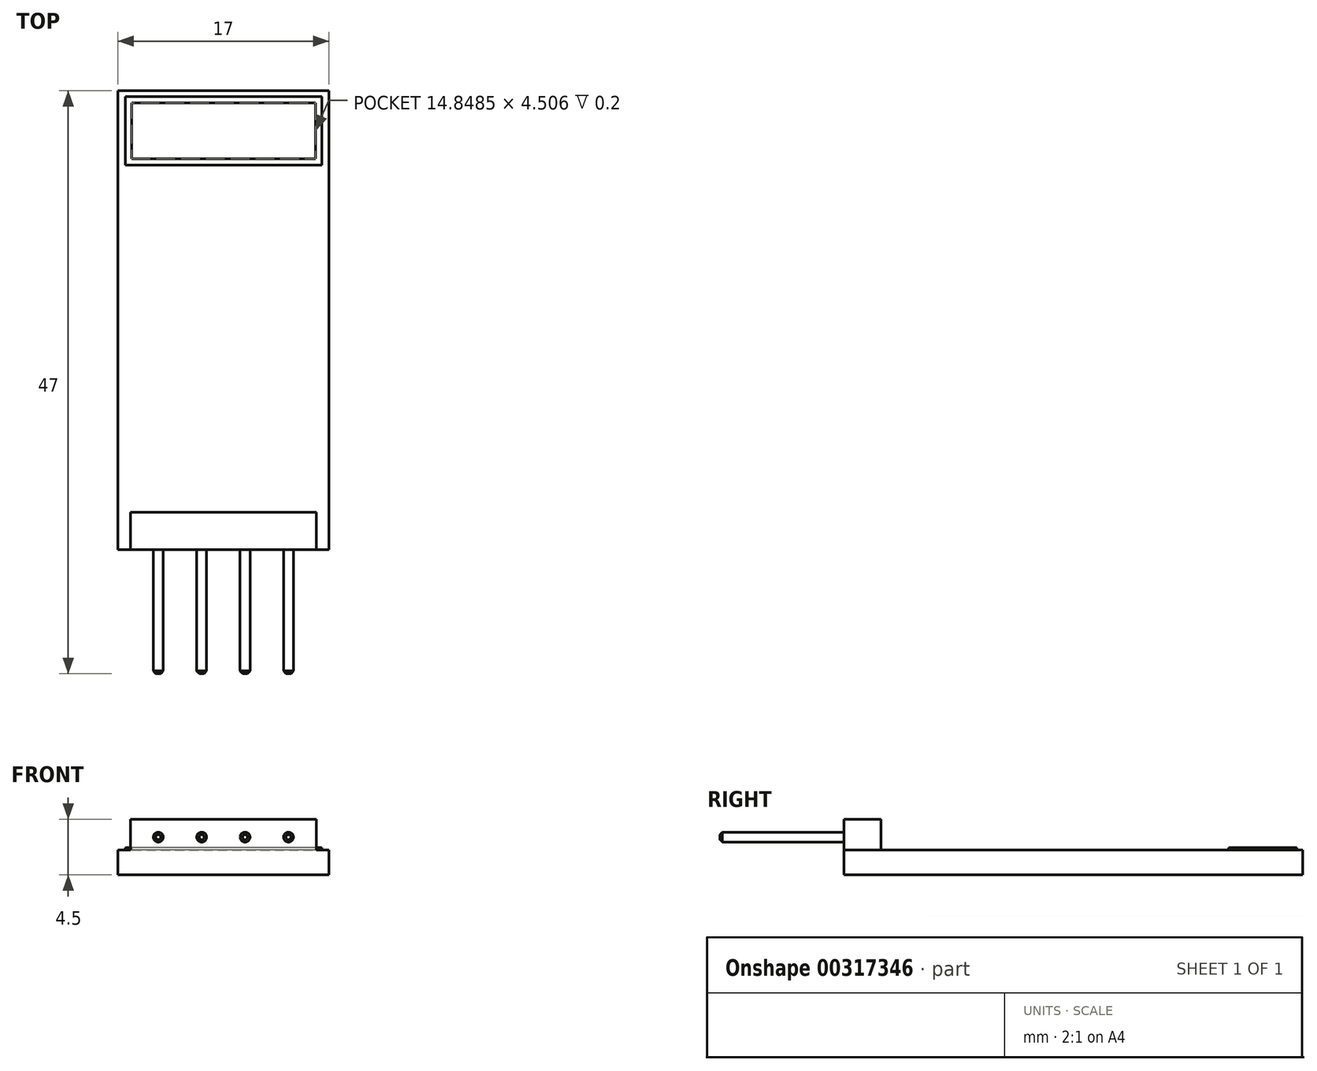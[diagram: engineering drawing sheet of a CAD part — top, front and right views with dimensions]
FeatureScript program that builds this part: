
annotation { "Feature Type Name" : "Feature", "Feature Type Description" : "" }
export const myFeature = defineFeature(function(context is Context, id is Id, definition is map)
    precondition{}
    {
        {
            var Q0;
            Q0=qCreatedBy(makeId("Top.planeOp"),FACE);
            var sketch = newSketch(context, id + "F0", { "sketchPlane" : qUnion([Q0])});
            skLineSegment(sketch, "E0.bottom", {"start": v(-8.5, 18.5) * mm, "end": v(8.5, 18.5) * mm});
            skLineSegment(sketch, "E0.top", {"start": v(-8.5, -18.5) * mm, "end": v(8.5, -18.5) * mm});
            skLineSegment(sketch, "E0.left", {"start": v(-8.5, 18.5) * mm, "end": v(-8.5, -18.5) * mm});
            skLineSegment(sketch, "E0.right", {"start": v(8.5, 18.5) * mm, "end": v(8.5, -18.5) * mm});
            skSolve(sketch);
        }
        {
            var Q0;
            Q0=makeQuery(id+"F0.imprint","IMPRINT",FACE,{"disambiguationData":[TD([[makeQuery(id+"F0.imprint","IMPRINT",EDGE,{"derivedFrom":sQuery(id+"F0.wireOp",EDGE,"E0.bottom")}),-1.0]])]});
            extrude(context, id + "F1", {"entities" : qUnion([Q0]), "endBound" : BoundingType.SYMMETRIC, "depth" : 2 * mm});
        }
        {
            var Q0;
            Q0=makeQuery(id+"F1.opExtrude","CAP_FACE",FACE,{"disambiguationData":[OSD([sQuery(id+"F0.wireOp",EDGE,"E0.bottom"),sQuery(id+"F0.wireOp",EDGE,"E0.top"),sQuery(id+"F0.wireOp",EDGE,"E0.left"),sQuery(id+"F0.wireOp",EDGE,"E0.right")])],"isStart":false});
            var sketch = newSketch(context, id + "F2", { "sketchPlane" : qUnion([Q0])});
            skLineSegment(sketch, "E1.bottom", {"start": v(-7.5, -18.5) * mm, "end": v(7.5, -18.5) * mm});
            skLineSegment(sketch, "E1.top", {"start": v(-7.5, -15.5) * mm, "end": v(7.5, -15.5) * mm});
            skLineSegment(sketch, "E1.left", {"start": v(-7.5, -18.5) * mm, "end": v(-7.5, -15.5) * mm});
            skLineSegment(sketch, "E1.right", {"start": v(7.5, -18.5) * mm, "end": v(7.5, -15.5) * mm});
            skSolve(sketch);
        }
        {
            var Q0;
            Q0=makeQuery(id+"F2.imprint","IMPRINT",FACE,{"disambiguationData":[TD([[makeQuery(id+"F2.imprint","IMPRINT",EDGE,{"derivedFrom":sQuery(id+"F2.wireOp",EDGE,"E1.bottom")}),1.0]])]});
            extrude(context, id + "F3", {"entities" : qUnion([Q0]), "operationType" : NewBodyOperationType.ADD, "depth" : 2.5 * mm});
        }
        {
            var Q0;
            Q0=makeQuery(id+"F3.boolean.opBoolean","MERGE",FACE,{"derivedFrom":[makeQuery(id+"F1.opExtrude","SWEPT_FACE",FACE,{"disambiguationData":[OSD([sQuery(id+"F0.wireOp",EDGE,"E0.top")])]}),makeQuery(id+"F3.opExtrude","SWEPT_FACE",FACE,{"disambiguationData":[OSD([sQuery(id+"F2.wireOp",EDGE,"E1.bottom")])]})]});
            var sketch = newSketch(context, id + "F4", { "sketchPlane" : qUnion([Q0])});
            skCircle(sketch, "E2", {"center": v(-5.25, 2.05) * mm, "radius": 0.4 * mm});
            skCircle(sketch, "E3.1.0.0", {"center": v(-1.75, 2.05) * mm, "radius": 0.4 * mm});
            skCircle(sketch, "E3.2.0.0", {"center": v(1.75, 2.05) * mm, "radius": 0.4 * mm});
            skCircle(sketch, "E3.3.0.0", {"center": v(5.25, 2.05) * mm, "radius": 0.4 * mm});
            skLineSegment(sketch, "E3.direction1", {"start": v(-5.25, 2.05) * mm, "end": v(-1.75, 2.05) * mm, "construction": true});
            skLineSegment(sketch, "E4", {"start": v(-5.25, 2.05) * mm, "end": v(-7.5, 2.05) * mm, "construction": true});
            skLineSegment(sketch, "E5", {"start": v(5.25, 2.05) * mm, "end": v(7.5, 2.05) * mm, "construction": true});
            skSolve(sketch);
        }
        {
            var Q0;
            Q0=makeQuery(id+"F4.imprint","IMPRINT",FACE,{"disambiguationData":[TD([[makeQuery(id+"F4.imprint","IMPRINT",EDGE,{"derivedFrom":sQuery(id+"F4.wireOp",EDGE,"E2")}),1.0]])]});
            var Q1;
            Q1=makeQuery(id+"F4.imprint","IMPRINT",FACE,{"disambiguationData":[TD([[makeQuery(id+"F4.imprint","IMPRINT",EDGE,{"derivedFrom":sQuery(id+"F4.wireOp",EDGE,"E3.1.0.0")}),1.0]])]});
            var Q2;
            Q2=makeQuery(id+"F4.imprint","IMPRINT",FACE,{"disambiguationData":[TD([[makeQuery(id+"F4.imprint","IMPRINT",EDGE,{"derivedFrom":sQuery(id+"F4.wireOp",EDGE,"E3.2.0.0")}),1.0]])]});
            var Q3;
            Q3=makeQuery(id+"F4.imprint","IMPRINT",FACE,{"disambiguationData":[TD([[makeQuery(id+"F4.imprint","IMPRINT",EDGE,{"derivedFrom":sQuery(id+"F4.wireOp",EDGE,"E3.3.0.0")}),1.0]])]});
            extrude(context, id + "F5", {"entities" : qUnion([Q0, Q1, Q2, Q3]), "operationType" : NewBodyOperationType.ADD, "depth" : 10 * mm});
        }
        {
            var Q0;
            Q0=makeQuery(id+"F5.opExtrude","CAP_EDGE",EDGE,{"disambiguationData":[OSD([sQuery(id+"F4.wireOp",EDGE,"E2")])],"isStart":false});
            var Q1;
            Q1=makeQuery(id+"F5.opExtrude","CAP_EDGE",EDGE,{"disambiguationData":[OSD([sQuery(id+"F4.wireOp",EDGE,"E3.1.0.0")])],"isStart":false});
            var Q2;
            Q2=makeQuery(id+"F5.opExtrude","CAP_EDGE",EDGE,{"disambiguationData":[OSD([sQuery(id+"F4.wireOp",EDGE,"E3.2.0.0")])],"isStart":false});
            var Q3;
            Q3=makeQuery(id+"F5.opExtrude","CAP_EDGE",EDGE,{"disambiguationData":[OSD([sQuery(id+"F4.wireOp",EDGE,"E3.3.0.0")])],"isStart":false});
            chamfer(context, id + "F6", {"entities" : qUnion([Q0, Q1, Q2, Q3]), "width" : 0.2 * mm, "tangentPropagation" : true});
        }
        {
            var Q0;
            Q0=makeQuery(id+"F1.opExtrude","CAP_FACE",FACE,{"disambiguationData":[OSD([sQuery(id+"F0.wireOp",EDGE,"E0.bottom"),sQuery(id+"F0.wireOp",EDGE,"E0.top"),sQuery(id+"F0.wireOp",EDGE,"E0.left"),sQuery(id+"F0.wireOp",EDGE,"E0.right")])],"isStart":false});
            var sketch = newSketch(context, id + "F7", { "sketchPlane" : qUnion([Q0])});
            skLineSegment(sketch, "E6.bottom", {"start": v(7.95, 18.02) * mm, "end": v(-7.9, 18.02) * mm});
            skLineSegment(sketch, "E6.top", {"start": v(7.95, 12.51) * mm, "end": v(-7.9, 12.51) * mm});
            skLineSegment(sketch, "E6.left", {"start": v(7.95, 18.02) * mm, "end": v(7.95, 12.51) * mm});
            skLineSegment(sketch, "E6.right", {"start": v(-7.9, 18.02) * mm, "end": v(-7.9, 12.51) * mm});
            skLineSegment(sketch, "E7.0", {"start": v(7.45, 17.52) * mm, "end": v(7.45, 13.01) * mm});
            skLineSegment(sketch, "E7.1", {"start": v(7.45, 17.52) * mm, "end": v(-7.4, 17.52) * mm});
            skLineSegment(sketch, "E7.2", {"start": v(-7.4, 17.52) * mm, "end": v(-7.4, 13.01) * mm});
            skLineSegment(sketch, "E7.3", {"start": v(7.45, 13.01) * mm, "end": v(-7.4, 13.01) * mm});
            skSolve(sketch);
        }
        {
            var Q0;
            Q0=makeQuery(id+"F7.imprint","IMPRINT",FACE,{"disambiguationData":[TD([[makeQuery(id+"F7.imprint","IMPRINT",EDGE,{"derivedFrom":sQuery(id+"F7.wireOp",EDGE,"E6.bottom")}),1.0]])]});
            extrude(context, id + "F8", {"entities" : qUnion([Q0]), "operationType" : NewBodyOperationType.ADD, "depth" : 0.2 * mm});
        }
    });
